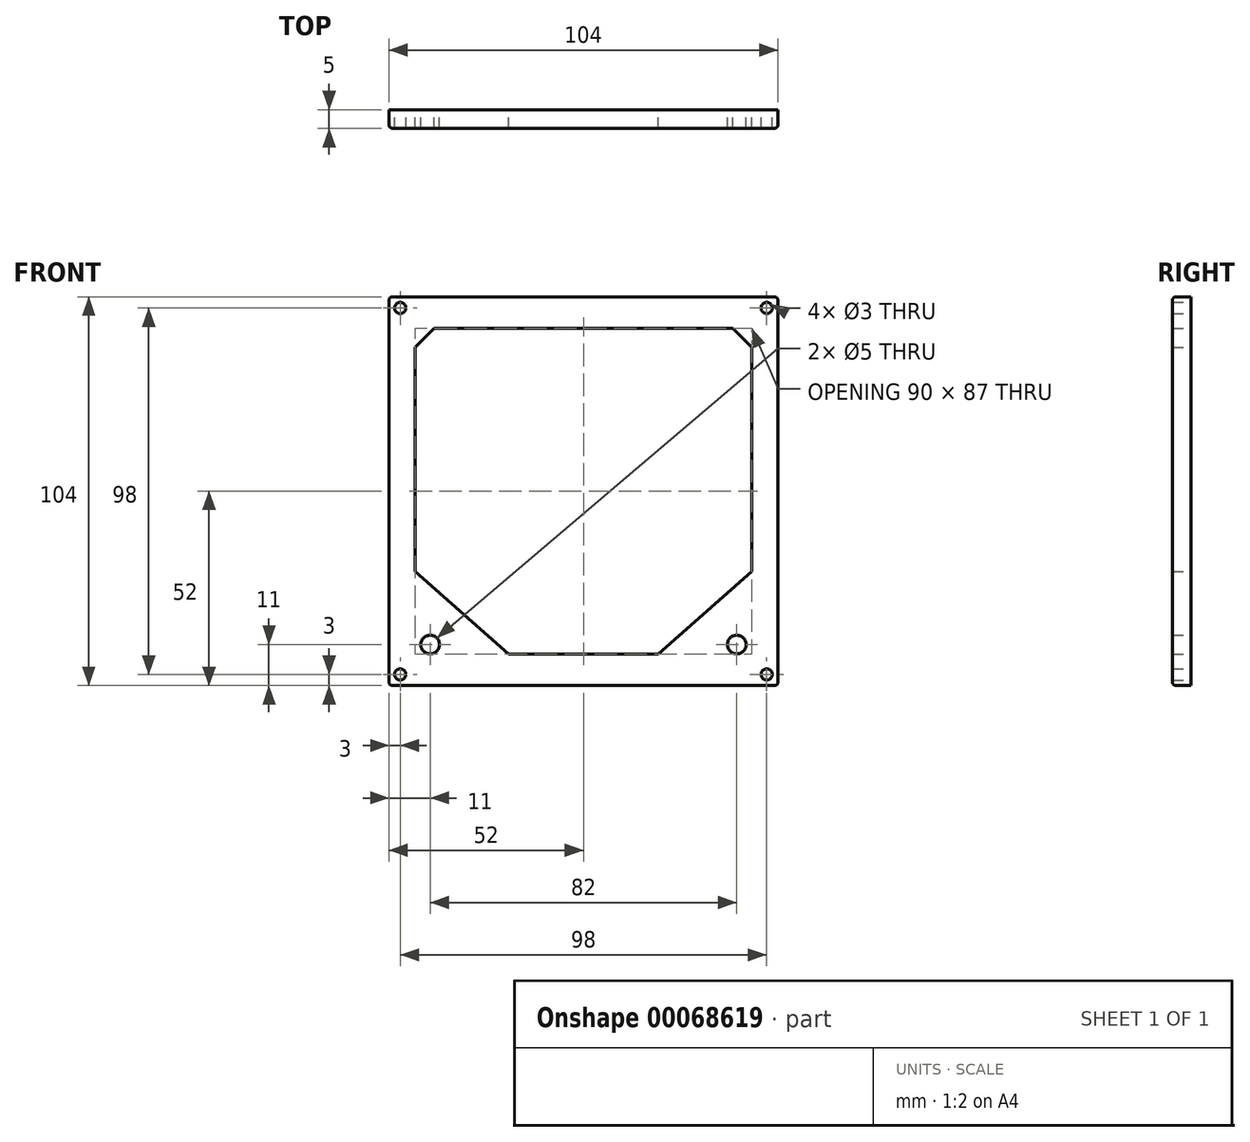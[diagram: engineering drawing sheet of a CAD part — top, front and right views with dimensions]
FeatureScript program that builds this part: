
annotation { "Feature Type Name" : "Feature", "Feature Type Description" : "" }
export const myFeature = defineFeature(function(context is Context, id is Id, definition is map)
    precondition{}
    {
        {
            var Q0;
            Q0=qCreatedBy(makeId("Front.planeOp"),FACE);
            var sketch = newSketch(context, id + "F0", { "sketchPlane" : qUnion([Q0])});
            skLineSegment(sketch, "E0.bottom", {"start": v(-52, 52) * mm, "end": v(52, 52) * mm});
            skLineSegment(sketch, "E0.top", {"start": v(-52, -52) * mm, "end": v(52, -52) * mm});
            skLineSegment(sketch, "E0.left", {"start": v(-52, 52) * mm, "end": v(-52, -52) * mm});
            skLineSegment(sketch, "E0.right", {"start": v(52, 52) * mm, "end": v(52, -52) * mm});
            skCircle(sketch, "E1", {"center": v(-49, 49) * mm, "radius": 1.5 * mm});
            skCircle(sketch, "E2", {"center": v(49, 49) * mm, "radius": 1.5 * mm});
            skCircle(sketch, "E3", {"center": v(-49, -49) * mm, "radius": 1.5 * mm});
            skCircle(sketch, "E4", {"center": v(49, -49) * mm, "radius": 1.5 * mm});
            skCircle(sketch, "E5", {"center": v(-41, -41) * mm, "radius": 2.5 * mm});
            skCircle(sketch, "E6", {"center": v(41, -41) * mm, "radius": 2.5 * mm});
            skSolve(sketch);
        }
        {
            var Q0;
            Q0=qCreatedBy(makeId("Front.planeOp"),FACE);
            var sketch = newSketch(context, id + "F1", { "sketchPlane" : qUnion([Q0])});
            skLineSegment(sketch, "E7", {"start": v(-40, 43.5) * mm, "end": v(40, 43.5) * mm});
            skLineSegment(sketch, "E8", {"start": v(40, 43.5) * mm, "end": v(45, 38.5) * mm});
            skLineSegment(sketch, "E9", {"start": v(45, 38.5) * mm, "end": v(45, -21.5) * mm});
            skLineSegment(sketch, "E10", {"start": v(45, -21.5) * mm, "end": v(20, -43.5) * mm});
            skLineSegment(sketch, "E11", {"start": v(20, -43.5) * mm, "end": v(-20, -43.5) * mm});
            skLineSegment(sketch, "E12", {"start": v(-20, -43.5) * mm, "end": v(-45, -21.5) * mm});
            skLineSegment(sketch, "E13", {"start": v(-45, -21.5) * mm, "end": v(-45, 38.5) * mm});
            skLineSegment(sketch, "E14", {"start": v(-45, 38.5) * mm, "end": v(-40, 43.5) * mm});
            skSolve(sketch);
        }
        {
            var Q0;
            Q0=makeQuery(id+"F0.imprint","IMPRINT",FACE,{"disambiguationData":[TD([[makeQuery(id+"F0.imprint","IMPRINT",EDGE,{"derivedFrom":sQuery(id+"F0.wireOp",EDGE,"E0.bottom")}),-1.0]])]});
            extrude(context, id + "F2", {"entities" : qUnion([Q0]), "depth" : 5 * mm});
        }
        {
            var Q0;
            Q0=qSketchRegion(id+"F1",true);
            var Q1;
            Q1=makeQuery(id+"F2.opExtrude","CAP_FACE",FACE,{"disambiguationData":[OSD([sQuery(id+"F0.wireOp",EDGE,"E0.bottom"),sQuery(id+"F0.wireOp",EDGE,"E0.top"),sQuery(id+"F0.wireOp",EDGE,"E0.left"),sQuery(id+"F0.wireOp",EDGE,"E0.right"),sQuery(id+"F0.wireOp",EDGE,"E1"),sQuery(id+"F0.wireOp",EDGE,"E2"),sQuery(id+"F0.wireOp",EDGE,"E3"),sQuery(id+"F0.wireOp",EDGE,"E4")])],"isStart":false});
            extrude(context, id + "F3", {"entities" : qUnion([Q0, Q1]), "operationType" : NewBodyOperationType.REMOVE, "depth" : 25 * mm});
        }
        {
            var Q0;
            Q0=makeQuery(id+"F2.opExtrude","SWEPT_EDGE",EDGE,{"disambiguationData":[OSD([sQuery(id+"F0.wireOp",EDGE,"E0.bottom"),sQuery(id+"F0.wireOp",EDGE,"E0.left")])]});
            var Q1;
            Q1=makeQuery(id+"F2.opExtrude","CAP_EDGE",EDGE,{"disambiguationData":[OSD([sQuery(id+"F0.wireOp",EDGE,"E0.left")])],"isStart":false});
            var Q2;
            Q2=makeQuery(id+"F2.opExtrude","CAP_EDGE",EDGE,{"disambiguationData":[OSD([sQuery(id+"F0.wireOp",EDGE,"E0.bottom")])],"isStart":false});
            var Q3;
            Q3=makeQuery(id+"F2.opExtrude","SWEPT_EDGE",EDGE,{"disambiguationData":[OSD([sQuery(id+"F0.wireOp",EDGE,"E0.top"),sQuery(id+"F0.wireOp",EDGE,"E0.left")])]});
            var Q4;
            Q4=makeQuery(id+"F2.opExtrude","CAP_EDGE",EDGE,{"disambiguationData":[OSD([sQuery(id+"F0.wireOp",EDGE,"E0.top")])],"isStart":false});
            var Q5;
            Q5=makeQuery(id+"F2.opExtrude","CAP_EDGE",EDGE,{"disambiguationData":[OSD([sQuery(id+"F0.wireOp",EDGE,"E0.right")])],"isStart":false});
            var Q6;
            Q6=makeQuery(id+"F2.opExtrude","SWEPT_EDGE",EDGE,{"disambiguationData":[OSD([sQuery(id+"F0.wireOp",EDGE,"E0.bottom"),sQuery(id+"F0.wireOp",EDGE,"E0.right")])]});
            var Q7;
            Q7=makeQuery(id+"F2.opExtrude","SWEPT_EDGE",EDGE,{"disambiguationData":[OSD([sQuery(id+"F0.wireOp",EDGE,"E0.top"),sQuery(id+"F0.wireOp",EDGE,"E0.right")])]});
            fillet(context, id + "F4", {"entities" : qUnion([Q0, Q1, Q2, Q3, Q4, Q5, Q6, Q7]), "radius" : 1 * mm, "tangentPropagation" : true, "allowEdgeOverflow" : false});
        }
    });
